# Revit family: P3847-09 3-100W INVRTED PENDANT
name_source: partatom
category: Lighting Fixtures
revit_build: Autodesk Revit Architecture 2012 (Build: 20110309_2315(x64)
units: mm (PartAtom-declared; Revit-internal decimal feet)

## types (1)
- P3847-09 3-100W INVRTED PENDANT
    Back Plate = Plated Brushed Nickel
    Ceiling Chain = Plated Brushed Nickel
    Celing chain length = 50.00"
    Default Elevation = 48.00"
    Description = Three-light inverted pendent with etched white oversized, bell-shaped glass bowl. Distinctive ebbing and flowing of squared scrolls and arms in Brushed Nickel finish.
    Family = Torino
    Glass = Default Light Source
    Lamp = Three
    Manufacturer = Progress Lighting
    Manufacturer Fax = (864)-678-1065
    Model = P3847-09
    Mounting = Ceiling Semi-Flush Mount
    Product Documentation Link = https://progresslighting.com
    Product Page URL = https://progresslighting.com
    URL = http://www.progresslighting.com
    Wattage Comments = 100W

## geometry (parser evidence)
native form markers: Sweep x7
no freeform markers — native parametric forms only
